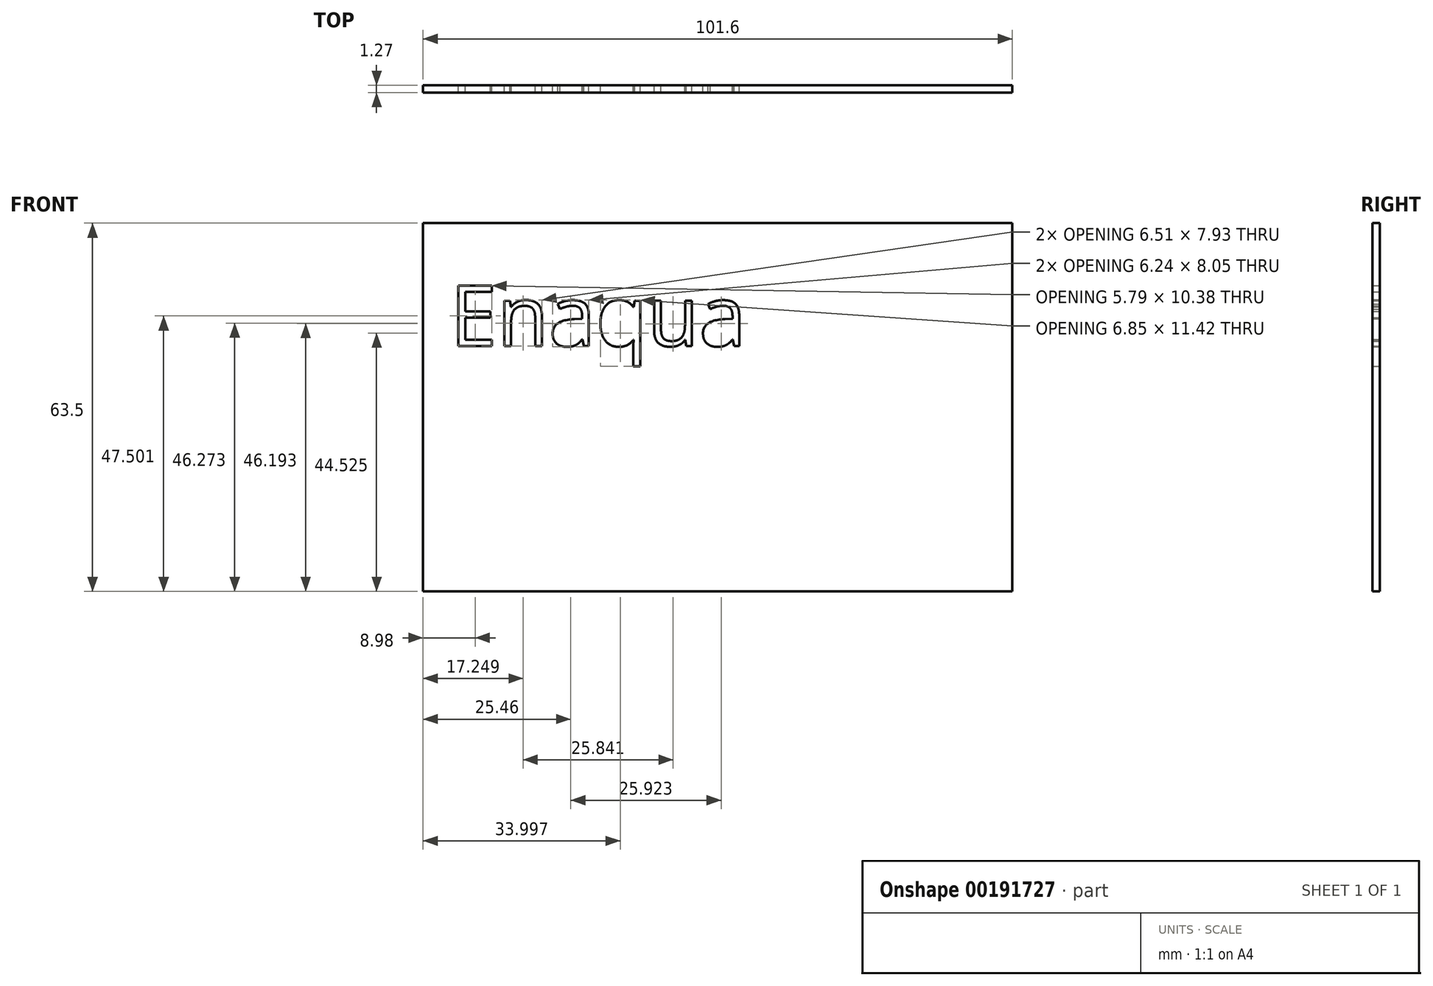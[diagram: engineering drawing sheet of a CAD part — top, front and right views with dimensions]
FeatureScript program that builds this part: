
annotation { "Feature Type Name" : "Feature", "Feature Type Description" : "" }
export const myFeature = defineFeature(function(context is Context, id is Id, definition is map)
    precondition{}
    {
        {
            var Q0;
            Q0=qCreatedBy(makeId("Front.planeOp"),FACE);
            var sketch = newSketch(context, id + "F0", { "sketchPlane" : qUnion([Q0])});
            skLineSegment(sketch, "E0.bottom", {"start": v(-65.92, 49.13) * mm, "end": v(35.68, 49.13) * mm});
            skLineSegment(sketch, "E0.top", {"start": v(-65.92, -14.37) * mm, "end": v(35.68, -14.37) * mm});
            skLineSegment(sketch, "E0.left", {"start": v(-65.92, 49.13) * mm, "end": v(-65.92, -14.37) * mm});
            skLineSegment(sketch, "E0.right", {"start": v(35.68, 49.13) * mm, "end": v(35.68, -14.37) * mm});
            skText(sketch, "E1", { "text": "Enaqua", "fontName": "OpenSans-Regular.ttf"});
            const initialGuessF0  = {"E1": [-0.06126, 0.02794, 1, 0, 0.01047]};
            skSetInitialGuess(sketch, initialGuessF0);
            skSolve(sketch);
        }
        {
            var Q0;
            Q0 = qSketchRegion(id + "F0", true);
            extrude(context, id + "F1", {"entities" : qUnion([Q0]), "depth" : 1.27 * mm});
        }
    });
